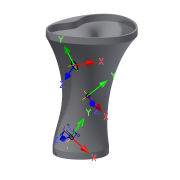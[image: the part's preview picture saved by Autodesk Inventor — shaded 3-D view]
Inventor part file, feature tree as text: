
AUTODESK INVENTOR PART (.ipt)
format: ipt  version: 2014 SP1 (Build 180222100, 222)  size: 1,840,128 bytes
history: native  units: in
note: dims shown in document units (in); Inventor stores cm internally (conversion verified against a paired STEP export)
features: other x36, sketch x7, plane x4, extrude x2, shell x1, imported_body x1
ambient origin geometry x8: Origin, YZ Plane, XZ Plane, XY Plane, X Axis, Y Axis, Z Axis, Center Point
bodies: Body1 (feature_tree)
feature tree (51):
  shell  "Shell1"  Thickness=0.3937in
  other  "Vase1"
  extrude  "Extrusion1"  Depth=3.937in
  extrude  "Extrusion2"  Depth=0.0984in
  plane  "Work Plane1"
  sketch  "Sketch3"  dims[d8772=0.0in d8773=0.0in d8774=0.0in d8775=0.0in d8776=0.0in d8777=0.0in]
  sketch  "3D Sketch1"
  plane  "Work Plane2"
  plane  "Work Plane3"
  plane  "Work Plane4"
  sketch  "Sketch4"  dims[d8778=0.0in d8779=0.0in d8780=0.0in d8781=0.0in d8782=0.0in d8783=0.0in]
  other  "Work Point2542"
  other  "Work Point2543"
  other  "Work Point2544"
  sketch  "Sketch5"  dims[d8784=0.0in d8785=0.0in d8786=0.0in d8787=0.0in d8788=0.0in d8789=0.0in]
  other  "Work Point1099"
  other  "Work Point1100"
  other  "Work Point1101"
  sketch  "Sketch369"
  other  "Work Point1096"
  other  "Work Point1097"
  other  "Work Point1098"
  other  "UCS1"
  other  "UCS2"
  other  "UCS3"
  imported_body  "Base1"
  sketch  "Sketch1"  dims[d2=0.3937in d3=0.0in d4=3.937in]
  sketch  "Sketch2"  dims[d8752=0.1575in d8753=0.0984in]
  other  "Project to Surface1"
  other  "Project to Surface2"
  other  "UCS1: YZ Plane"
  other  "UCS1: XZ Plane"
  other  "UCS1: XY Plane"
  other  "UCS1: X Axis"
  other  "UCS1: Y Axis"
  other  "UCS1: Z Axis"
  other  "UCS1: Center Point"
  other  "UCS2: YZ Plane"
  other  "UCS2: XZ Plane"
  other  "UCS2: XY Plane"
  other  "UCS2: X Axis"
  other  "UCS2: Y Axis"
  other  "UCS2: Z Axis"
  other  "UCS2: Center Point"
  other  "UCS3: YZ Plane"
  other  "UCS3: XZ Plane"
  other  "UCS3: XY Plane"
  other  "UCS3: X Axis"
  other  "UCS3: Y Axis"
  other  "UCS3: Z Axis"
  other  "UCS3: Center Point"
